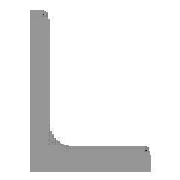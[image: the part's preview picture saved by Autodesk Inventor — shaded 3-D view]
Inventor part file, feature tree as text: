
AUTODESK INVENTOR PART (.ipt)
format: ipt  version: 2024.1 (Build 281209000, 209)  size: 120,320 bytes
history: native  units: mm (DEFAULTED — no unit token found)
features: other x4, sketch x1, plane x1
ambient origin geometry x8: Origin, YZ Plane, XZ Plane, XY Plane, X Axis, Y Axis, Z Axis, Center Point
bodies: Solid1 (feature_tree), Body (feature_tree)
feature tree (6):
  parser-record x1  (decoder bookkeeping rows leaked as tree rows — omitted from the tree; the rows remain in map.json)
  other  "Driven Length"
  other  "Start Plane"
  other  "End Plane"
  sketch  "Sketch3"  dims[d0=28.702mm d1=28.702mm d2=3.175mm d3=3.175mm d4=1200.0mm d5=0.0mm d10=0.0mm d11=0.0mm d12=-0.0mm d13=1200.0mm d14=2.286mm d15=1.27mm d16=90.0deg d17=1200.0mm]
  plane  "Work Plane3"
